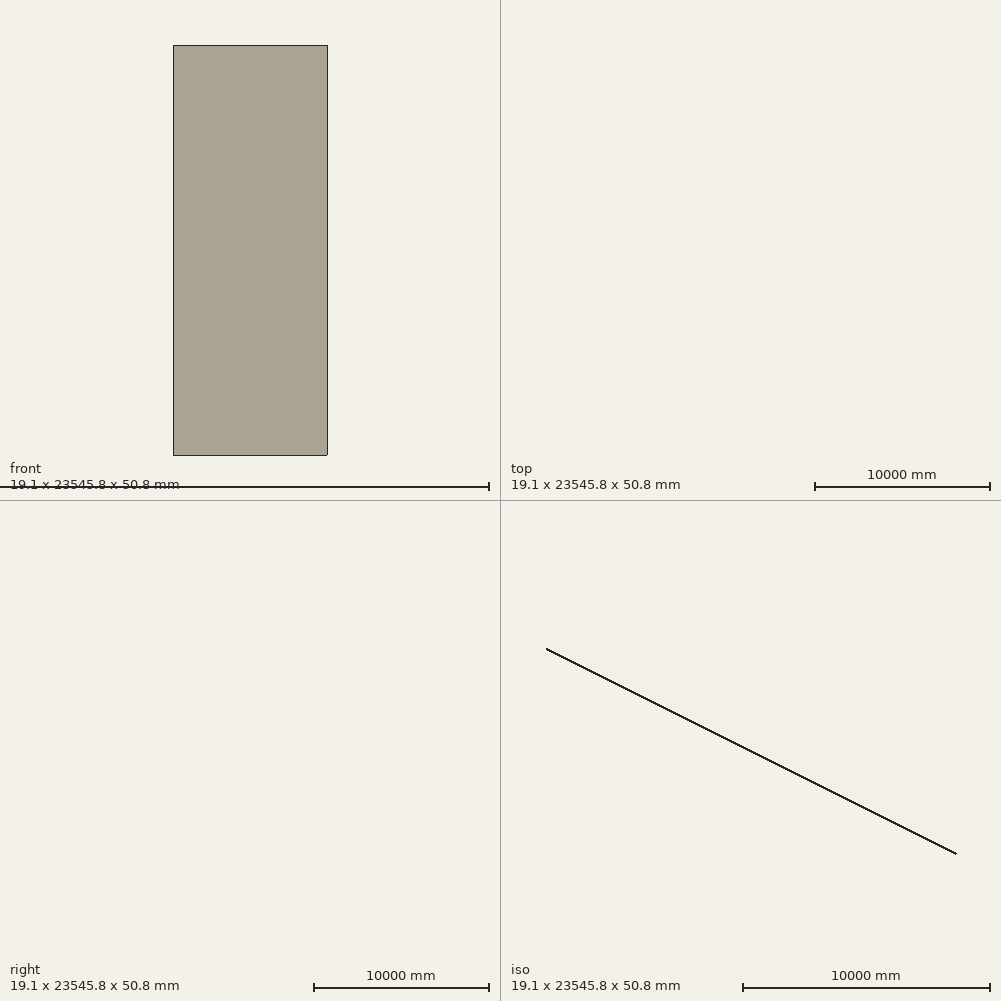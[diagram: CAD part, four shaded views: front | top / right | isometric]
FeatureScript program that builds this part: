
annotation { "Feature Type Name" : "Feature", "Feature Type Description" : "" }
export const myFeature = defineFeature(function(context is Context, id is Id, definition is map)
    precondition{}
    {
        {
            var Q0;
            Q0=qCreatedBy(makeId("Front.planeOp"),FACE);
            var sketch = newSketch(context, id + "F0", { "sketchPlane" : qUnion([Q0])});
            skLineSegment(sketch, "E0", {"start": v(0, 0) * mm, "end": v(19.05, 0) * mm});
            skLineSegment(sketch, "E1", {"start": v(0, 0) * mm, "end": v(0, -50.8) * mm});
            skLineSegment(sketch, "E2", {"start": v(0, -50.8) * mm, "end": v(19.05, -50.8) * mm});
            skLineSegment(sketch, "E3", {"start": v(19.05, -50.8) * mm, "end": v(19.05, 0) * mm});
            skSolve(sketch);
        }
        {
            var Q0;
            Q0=makeQuery(id+"F0.imprint","IMPRINT",FACE,{"disambiguationData":[TD([[makeQuery(id+"F0.imprint","IMPRINT",EDGE,{"derivedFrom":sQuery(id+"F0.wireOp",EDGE,"E0")}),-1.0]])]});
            extrude(context, id + "F1", {"entities" : qUnion([Q0]), "oppositeDirection" : true, "depth" : 23545.8 * mm, "offsetDistance" : 25.4 * mm});
        }
    });
